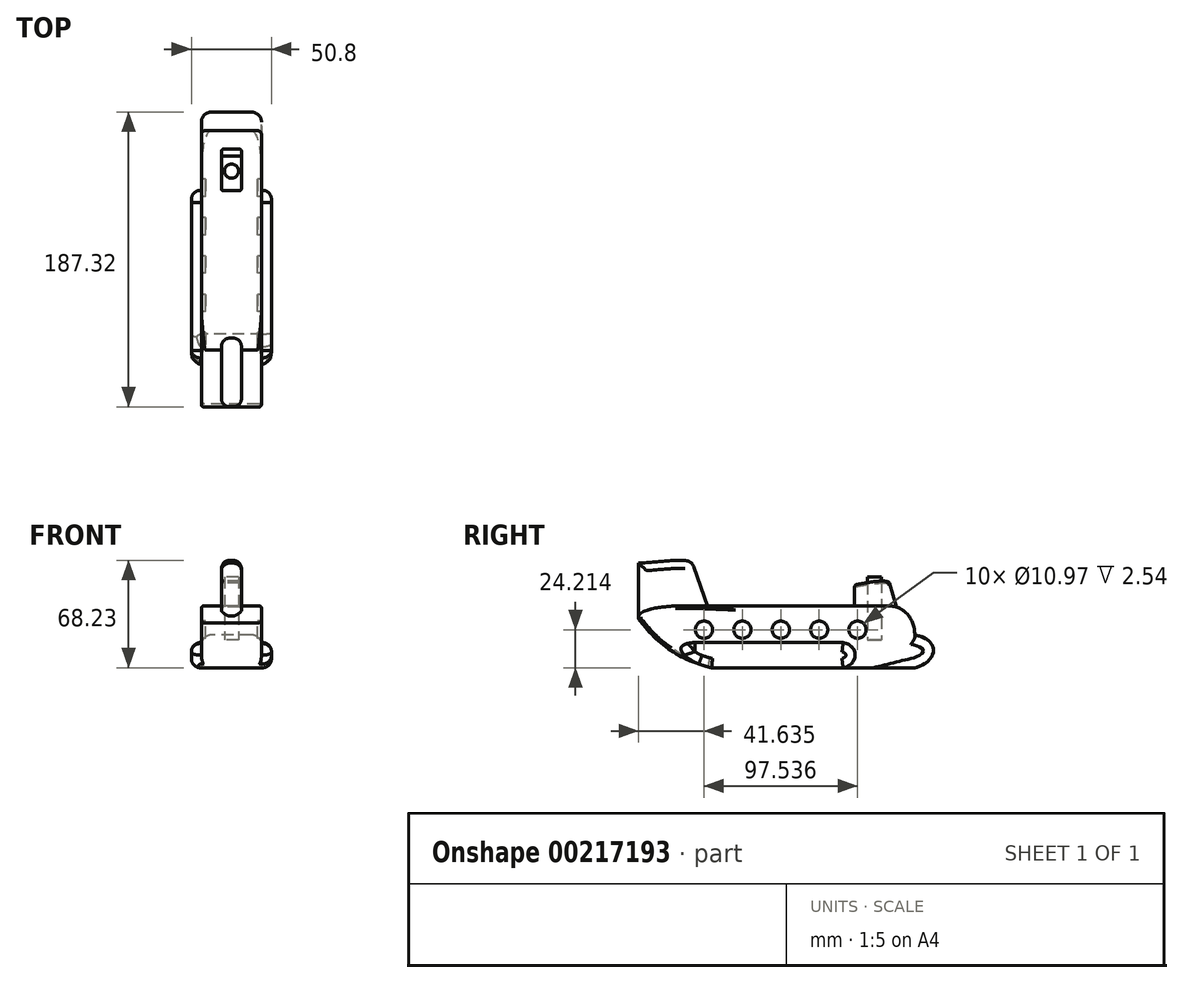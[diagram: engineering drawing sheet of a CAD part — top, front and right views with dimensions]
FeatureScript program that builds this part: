
annotation { "Feature Type Name" : "Feature", "Feature Type Description" : "" }
export const myFeature = defineFeature(function(context is Context, id is Id, definition is map)
    precondition{}
    {
        {
            var Q0;
            Q0=qCreatedBy(makeId("Right.planeOp"),FACE);
            var sketch = newSketch(context, id + "F0", { "sketchPlane" : qUnion([Q0])});
            skLineSegment(sketch, "E0", {"start": v(-54.05, 21.64) * mm, "end": v(-53.32, 21.64) * mm});
            skFitSpline(sketch, "E1", {"points": [v(82.46, 21.64) * mm, v(98.66, 3.26) * mm], "startDerivative": vector(30.2, 0) * mm, "endDerivative": vector(0, -27.99) * mm});
            skFitSpline(sketch, "E2", {"points": [v(98.66, 3.26) * mm, v(98.66, -17.65) * mm], "startDerivative": vector(52.2, -9.77) * mm, "endDerivative": vector(-41.98, -10.31) * mm});
            skLineSegment(sketch, "E3", {"start": v(98.66, -17.65) * mm, "end": v(-30.48, -17.65) * mm});
            skFitSpline(sketch, "E4", {"points": [v(-30.48, -17.65) * mm, v(-74.85, 11.03) * mm], "startDerivative": vector(-71.45, 18.41) * mm, "endDerivative": vector(-25.78, 33.09) * mm});
            skFitSpline(sketch, "E5", {"points": [v(-74.85, 11.03) * mm, v(-40.72, 21.64) * mm], "startDerivative": vector(-25.04, 22.1) * mm, "endDerivative": vector(70.71, -2.8) * mm});
            skLineSegment(sketch, "E6.trimOffspring", {"start": v(-40.72, 21.64) * mm, "end": v(82.46, 21.64) * mm});
            skLineSegment(sketch, "E7", {"start": v(-76.72, 15.19) * mm, "end": v(-76.72, 48.86) * mm});
            skFitSpline(sketch, "E8", {"points": [v(-76.72, 48.86) * mm, v(-42.85, 50.14) * mm], "startDerivative": vector(44.89, 2.47) * mm, "endDerivative": vector(37.78, -3.72) * mm});
            skLineSegment(sketch, "E9", {"start": v(86.92, 21) * mm, "end": v(82.56, 36.28) * mm});
            skFitSpline(sketch, "E10", {"points": [v(82.56, 36.28) * mm, v(60.49, 34.99) * mm], "startDerivative": vector(-3.5, 5.38) * mm, "endDerivative": vector(-44.45, -9.24) * mm});
            skLineSegment(sketch, "E11", {"start": v(60.49, 34.99) * mm, "end": v(60.49, 21.64) * mm});
            skLineSegment(sketch, "E12", {"start": v(-33.14, 21.64) * mm, "end": v(-41.5, 46.17) * mm});
            skArc(sketch, "E13.filletArc", {"start": v(-41.5, 46.17) * mm, "mid": v(-43.68, 49.2) * mm, "end": v(-47.18, 50.47) * mm});
            skLineSegment(sketch, "E14", {"start": v(-40.94, -1.55) * mm, "end": v(53.12, -1.55) * mm});
            skCircle(sketch, "E15", {"center": v(62.32, 6.56) * mm, "radius": 5.49 * mm});
            skLineSegment(sketch, "E16", {"start": v(62.32, 6.56) * mm, "end": v(-57.86, 6.56) * mm, "construction": true});
            skCircle(sketch, "E17.1.0.0", {"center": v(37.94, 6.56) * mm, "radius": 5.49 * mm});
            skCircle(sketch, "E17.2.0.0", {"center": v(13.55, 6.56) * mm, "radius": 5.49 * mm});
            skCircle(sketch, "E17.3.0.0", {"center": v(-10.83, 6.56) * mm, "radius": 5.49 * mm});
            skCircle(sketch, "E17.4.0.0", {"center": v(-35.22, 6.56) * mm, "radius": 5.49 * mm});
            skLineSegment(sketch, "E17.direction1", {"start": v(62.32, 6.56) * mm, "end": v(37.94, 6.56) * mm, "construction": true});
            skFitSpline(sketch, "E18", {"points": [v(53.12, -1.55) * mm, v(53.12, -17.65) * mm], "startDerivative": vector(30.45, -6.6) * mm, "endDerivative": vector(-30.94, -7.28) * mm});
            skFitSpline(sketch, "E19", {"points": [v(-40.94, -1.55) * mm, v(-30.48, -17.65) * mm], "startDerivative": vector(-54.61, -2.68) * mm, "endDerivative": vector(47.15, -9.25) * mm});
            skSolve(sketch);
        }
        {
            var Q0;
            {var subQ14=sQuery(id+"F0.wireOp",EDGE,"E2");Q0=makeQuery(id+"F0.imprint","IMPRINT",FACE,{"disambiguationData":[TD([[makeQuery(id+"F0.imprint","IMPRINT",EDGE,{"derivedFrom":subQ14}),-1.0]])]});}
            extrude(context, id + "F1", {"entities" : qUnion([Q0]), "endBound" : BoundingType.SYMMETRIC, "depth" : 38.1 * mm});
        }
        {
            var Q0;
            {var subQ1=sQuery(id+"F0.wireOp",EDGE,"E14");Q0=makeQuery(id+"F0.imprint","IMPRINT",FACE,{"disambiguationData":[TD([[makeQuery(id+"F0.imprint","IMPRINT",EDGE,{"derivedFrom":subQ1}),-1.0]])]});}
            extrude(context, id + "F2", {"entities" : qUnion([Q0]), "operationType" : NewBodyOperationType.ADD, "endBound" : BoundingType.SYMMETRIC, "depth" : 50.8 * mm});
        }
        {
            var Q0;
            {var subQ0=sQuery(id+"F0.wireOp",EDGE,"E7");Q0=makeQuery(id+"F0.imprint","IMPRINT",FACE,{"disambiguationData":[TD([[makeQuery(id+"F0.imprint","IMPRINT",EDGE,{"derivedFrom":subQ0}),-1.0]])]});}
            var Q1;
            {var subQ0=sQuery(id+"F0.wireOp",EDGE,"E9");Q1=makeQuery(id+"F0.imprint","IMPRINT",FACE,{"disambiguationData":[TD([[makeQuery(id+"F0.imprint","IMPRINT",EDGE,{"derivedFrom":subQ0}),1.0]])]});}
            extrude(context, id + "F3", {"entities" : qUnion([Q0, Q1]), "operationType" : NewBodyOperationType.ADD, "endBound" : BoundingType.SYMMETRIC, "depth" : 12.7 * mm});
        }
        {
            var Q0;
            Q0=makeQuery(id+"F0.imprint","IMPRINT",FACE,{"disambiguationData":[TD([[makeQuery(id+"F0.imprint","IMPRINT",EDGE,{"derivedFrom":sQuery(id+"F0.wireOp",EDGE,"E17.3.0.0")}),1.0]])]});
            var Q1;
            Q1=makeQuery(id+"F0.imprint","IMPRINT",FACE,{"disambiguationData":[TD([[makeQuery(id+"F0.imprint","IMPRINT",EDGE,{"derivedFrom":sQuery(id+"F0.wireOp",EDGE,"E17.2.0.0")}),1.0]])]});
            var Q2;
            Q2=makeQuery(id+"F0.imprint","IMPRINT",FACE,{"disambiguationData":[TD([[makeQuery(id+"F0.imprint","IMPRINT",EDGE,{"derivedFrom":sQuery(id+"F0.wireOp",EDGE,"E17.1.0.0")}),1.0]])]});
            var Q3;
            Q3=makeQuery(id+"F0.imprint","IMPRINT",FACE,{"disambiguationData":[TD([[makeQuery(id+"F0.imprint","IMPRINT",EDGE,{"derivedFrom":sQuery(id+"F0.wireOp",EDGE,"E15")}),1.0]])]});
            var Q4;
            Q4=makeQuery(id+"F0.imprint","IMPRINT",FACE,{"disambiguationData":[TD([[makeQuery(id+"F0.imprint","IMPRINT",EDGE,{"derivedFrom":sQuery(id+"F0.wireOp",EDGE,"E17.4.0.0")}),1.0]])]});
            extrude(context, id + "F4", {"entities" : qUnion([Q0, Q1, Q2, Q3, Q4]), "operationType" : NewBodyOperationType.ADD, "endBound" : BoundingType.SYMMETRIC, "depth" : 33.02 * mm});
        }
        {
            var Q0;
            Q0=makeQuery(id+"F2.opExtrude","CAP_EDGE",EDGE,{"disambiguationData":[OSD([sQuery(id+"F0.wireOp",EDGE,"E14")])],"isStart":false});
            var Q1;
            Q1=makeQuery(id+"F2.opExtrude","CAP_EDGE",EDGE,{"disambiguationData":[OSD([sQuery(id+"F0.wireOp",EDGE,"E19")])],"isStart":false});
            var Q2;
            Q2=makeQuery(id+"F2.opExtrude","CAP_FACE",FACE,{"disambiguationData":[OSD([sQuery(id+"F0.wireOp",EDGE,"E3"),sQuery(id+"F0.wireOp",EDGE,"E4"),sQuery(id+"F0.wireOp",EDGE,"E14"),sQuery(id+"F0.wireOp",EDGE,"E18"),sQuery(id+"F0.wireOp",EDGE,"E19")])],"isStart":false});
            var Q3;
            Q3=makeQuery(id+"F2.opExtrude","CAP_EDGE",EDGE,{"disambiguationData":[OSD([sQuery(id+"F0.wireOp",EDGE,"E19")])],"isStart":true});
            var Q4;
            Q4=makeQuery(id+"F2.opExtrude","CAP_EDGE",EDGE,{"disambiguationData":[OSD([sQuery(id+"F0.wireOp",EDGE,"E14")])],"isStart":true});
            var Q5;
            Q5=makeQuery(id+"F2.opExtrude","CAP_EDGE",EDGE,{"disambiguationData":[OSD([sQuery(id+"F0.wireOp",EDGE,"E18")])],"isStart":true});
            var Q6;
            Q6=makeQuery(id+"F2.opExtrude","CAP_EDGE",EDGE,{"disambiguationData":[OSD([sQuery(id+"F0.wireOp",EDGE,"E3")])],"isStart":true});
            fillet(context, id + "F5", {"entities" : qUnion([Q0, Q1, Q2, Q3, Q4, Q5, Q6]), "radius" : 5.84 * mm, "tangentPropagation" : true, "allowEdgeOverflow" : false});
        }
        {
            var Q0;
            Q0=makeQuery(id+"F1.opExtrude","CAP_EDGE",EDGE,{"disambiguationData":[OSD([sQuery(id+"F0.wireOp",EDGE,"E6.trimOffspring")])],"isStart":false});
            var Q1;
            Q1=makeQuery(id+"F1.opExtrude","CAP_EDGE",EDGE,{"disambiguationData":[OSD([sQuery(id+"F0.wireOp",EDGE,"E6.trimOffspring")])],"isStart":true});
            fillet(context, id + "F6", {"entities" : qUnion([Q0, Q1]), "radius" : 2.54 * mm, "tangentPropagation" : true, "allowEdgeOverflow" : false});
        }
        {
            var Q0;
            Q0=makeQuery(id+"F3.opExtrude","CAP_EDGE",EDGE,{"disambiguationData":[OSD([sQuery(id+"F0.wireOp",EDGE,"E7")])],"isStart":true});
            var Q1;
            Q1=makeQuery(id+"F3.opExtrude","CAP_EDGE",EDGE,{"disambiguationData":[OSD([sQuery(id+"F0.wireOp",EDGE,"E7")])],"isStart":false});
            var Q2;
            Q2=makeQuery(id+"F3.opExtrude","CAP_EDGE",EDGE,{"disambiguationData":[OSD([sQuery(id+"F0.wireOp",EDGE,"E12")])],"isStart":false});
            var Q3;
            Q3=makeQuery(id+"F3.opExtrude","CAP_EDGE",EDGE,{"disambiguationData":[OSD([sQuery(id+"F0.wireOp",EDGE,"E12")])],"isStart":true});
            fillet(context, id + "F7", {"entities" : qUnion([Q0, Q1, Q2, Q3]), "radius" : 5.08 * mm, "tangentPropagation" : true, "allowEdgeOverflow" : false});
        }
        {
            var Q0;
            Q0=makeQuery(id+"F3.opExtrude","CAP_EDGE",EDGE,{"disambiguationData":[OSD([sQuery(id+"F0.wireOp",EDGE,"E10")])],"isStart":false});
            var Q1;
            Q1=makeQuery(id+"F3.opExtrude","CAP_EDGE",EDGE,{"disambiguationData":[OSD([sQuery(id+"F0.wireOp",EDGE,"E11")])],"isStart":false});
            var Q2;
            Q2=makeQuery(id+"F3.opExtrude","CAP_EDGE",EDGE,{"disambiguationData":[OSD([sQuery(id+"F0.wireOp",EDGE,"E9")])],"isStart":false});
            var Q3;
            Q3=makeQuery(id+"F3.opExtrude","CAP_EDGE",EDGE,{"disambiguationData":[OSD([sQuery(id+"F0.wireOp",EDGE,"E9")])],"isStart":true});
            var Q4;
            Q4=makeQuery(id+"F3.opExtrude","CAP_EDGE",EDGE,{"disambiguationData":[OSD([sQuery(id+"F0.wireOp",EDGE,"E10")])],"isStart":true});
            var Q5;
            Q5=makeQuery(id+"F3.opExtrude","CAP_EDGE",EDGE,{"disambiguationData":[OSD([sQuery(id+"F0.wireOp",EDGE,"E11")])],"isStart":true});
            var Q6;
            Q6=makeQuery(id+"F3.opExtrude","SWEPT_EDGE",EDGE,{"disambiguationData":[OSD([sQuery(id+"F0.wireOp",EDGE,"E10"),sQuery(id+"F0.wireOp",EDGE,"E11")])]});
            fillet(context, id + "F8", {"entities" : qUnion([Q0, Q1, Q2, Q3, Q4, Q5, Q6]), "radius" : 1.27 * mm, "tangentPropagation" : true, "allowEdgeOverflow" : false});
        }
        {
            var Q0;
            Q0=makeQuery(id+"F1.opExtrude","CAP_EDGE",EDGE,{"disambiguationData":[OSD([sQuery(id+"F0.wireOp",EDGE,"E2")])],"isStart":false});
            var Q1;
            Q1=makeQuery(id+"F1.opExtrude","CAP_EDGE",EDGE,{"disambiguationData":[OSD([sQuery(id+"F0.wireOp",EDGE,"E2")])],"isStart":true});
            fillet(context, id + "F9", {"entities" : qUnion([Q0, Q1]), "radius" : 6.35 * mm, "tangentPropagation" : true, "allowEdgeOverflow" : false});
        }
        {
            var Q0;
            Q0=makeQuery(id+"F1.opExtrude","CAP_EDGE",EDGE,{"disambiguationData":[OSD([sQuery(id+"F0.wireOp",EDGE,"E4")])],"isStart":true});
            var Q1;
            Q1=makeQuery(id+"F1.opExtrude","CAP_EDGE",EDGE,{"disambiguationData":[OSD([sQuery(id+"F0.wireOp",EDGE,"E4")])],"isStart":false});
            fillet(context, id + "F10", {"entities" : qUnion([Q0, Q1]), "radius" : 1.52 * mm, "tangentPropagation" : true, "allowEdgeOverflow" : false});
        }
        {
            var Q0;
            Q0=makeQuery(id+"F1.opExtrude","CAP_EDGE",EDGE,{"disambiguationData":[OSD([sQuery(id+"F0.wireOp",EDGE,"E5")])],"isStart":true});
            var Q1;
            Q1=makeQuery(id+"F1.opExtrude","CAP_EDGE",EDGE,{"disambiguationData":[OSD([sQuery(id+"F0.wireOp",EDGE,"E5")])],"isStart":false});
            fillet(context, id + "F11", {"entities" : qUnion([Q0, Q1]), "radius" : 1.52 * mm, "tangentPropagation" : true, "allowEdgeOverflow" : false});
        }
        {
            var Q0;
            Q0=qCreatedBy(makeId("Top.planeOp"),FACE);
            var sketch = newSketch(context, id + "F12", { "sketchPlane" : qUnion([Q0])});
            skCircle(sketch, "E20", {"center": v(0, 72.93) * mm, "radius": 4.48 * mm});
            skSolve(sketch);
        }
        {
            var Q0;
            Q0=makeQuery(id+"F12.imprint","IMPRINT",FACE,{"disambiguationData":[TD([[makeQuery(id+"F12.imprint","IMPRINT",EDGE,{"derivedFrom":sQuery(id+"F12.wireOp",EDGE,"E20")}),1.0]])]});
            var Q1;
            Q1=sQuery(id+"F12.wireOp",EDGE,"E20");
            extrude(context, id + "F13", {"entities" : qUnion([Q0]), "surfaceEntities" : qUnion([Q1]), "depth" : 40.13 * mm});
        }
    });
